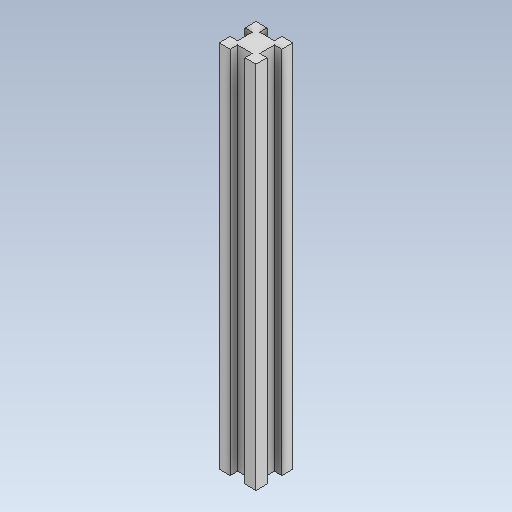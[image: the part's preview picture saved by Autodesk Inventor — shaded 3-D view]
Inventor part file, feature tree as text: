
AUTODESK INVENTOR PART (.ipt)
format: ipt  version: 2021 (Build 250183000, 183)  size: 119,296 bytes
history: native  units: mm
features: other x1, extrude x1, sketch x1
ambient origin geometry x8: Origin, YZ Plane, XZ Plane, XY Plane, X Axis, Y Axis, Z Axis, Center Point
bodies: Body1 (feature_tree)
feature tree (3):
  other  "Bryła1"
  extrude  "Wyciągnięcie proste1"  Depth=50.0mm
  sketch  "Szkic1"
